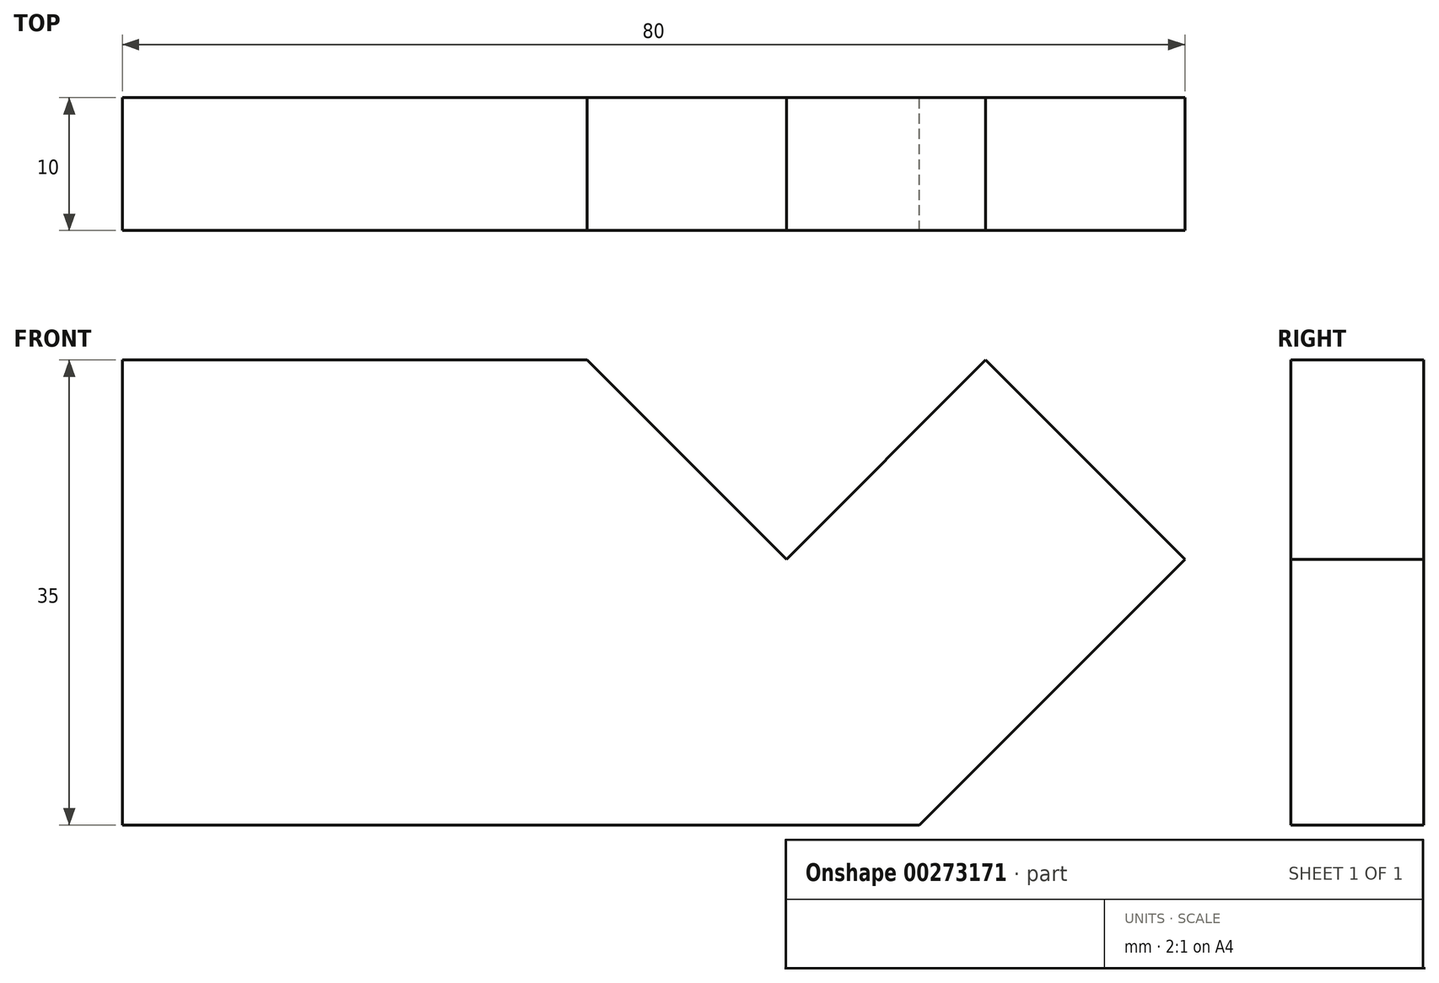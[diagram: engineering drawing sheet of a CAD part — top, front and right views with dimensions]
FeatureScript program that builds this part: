
annotation { "Feature Type Name" : "Feature", "Feature Type Description" : "" }
export const myFeature = defineFeature(function(context is Context, id is Id, definition is map)
    precondition{}
    {
        {
            var Q0;
            Q0=qCreatedBy(makeId("Front.planeOp"),FACE);
            var sketch = newSketch(context, id + "F0", { "sketchPlane" : qUnion([Q0])});
            skLineSegment(sketch, "E0", {"start": v(0, 0) * mm, "end": v(60, 0) * mm});
            skLineSegment(sketch, "E1", {"start": v(0, 0) * mm, "end": v(0, 35) * mm});
            skLineSegment(sketch, "E2", {"start": v(0, 35) * mm, "end": v(35, 35) * mm});
            skLineSegment(sketch, "E3", {"start": v(35, 35) * mm, "end": v(50, 20) * mm});
            skLineSegment(sketch, "E4", {"start": v(50, 20) * mm, "end": v(65, 35) * mm});
            skLineSegment(sketch, "E5", {"start": v(65, 35) * mm, "end": v(80, 20) * mm});
            skLineSegment(sketch, "E6", {"start": v(80, 20) * mm, "end": v(60, 0) * mm});
            skSolve(sketch);
        }
        {
            var Q0;
            Q0 = qSketchRegion(id + "F0", true);
            extrude(context, id + "F1", {"entities" : qUnion([Q0]), "depth" : 10 * mm});
        }
    });
